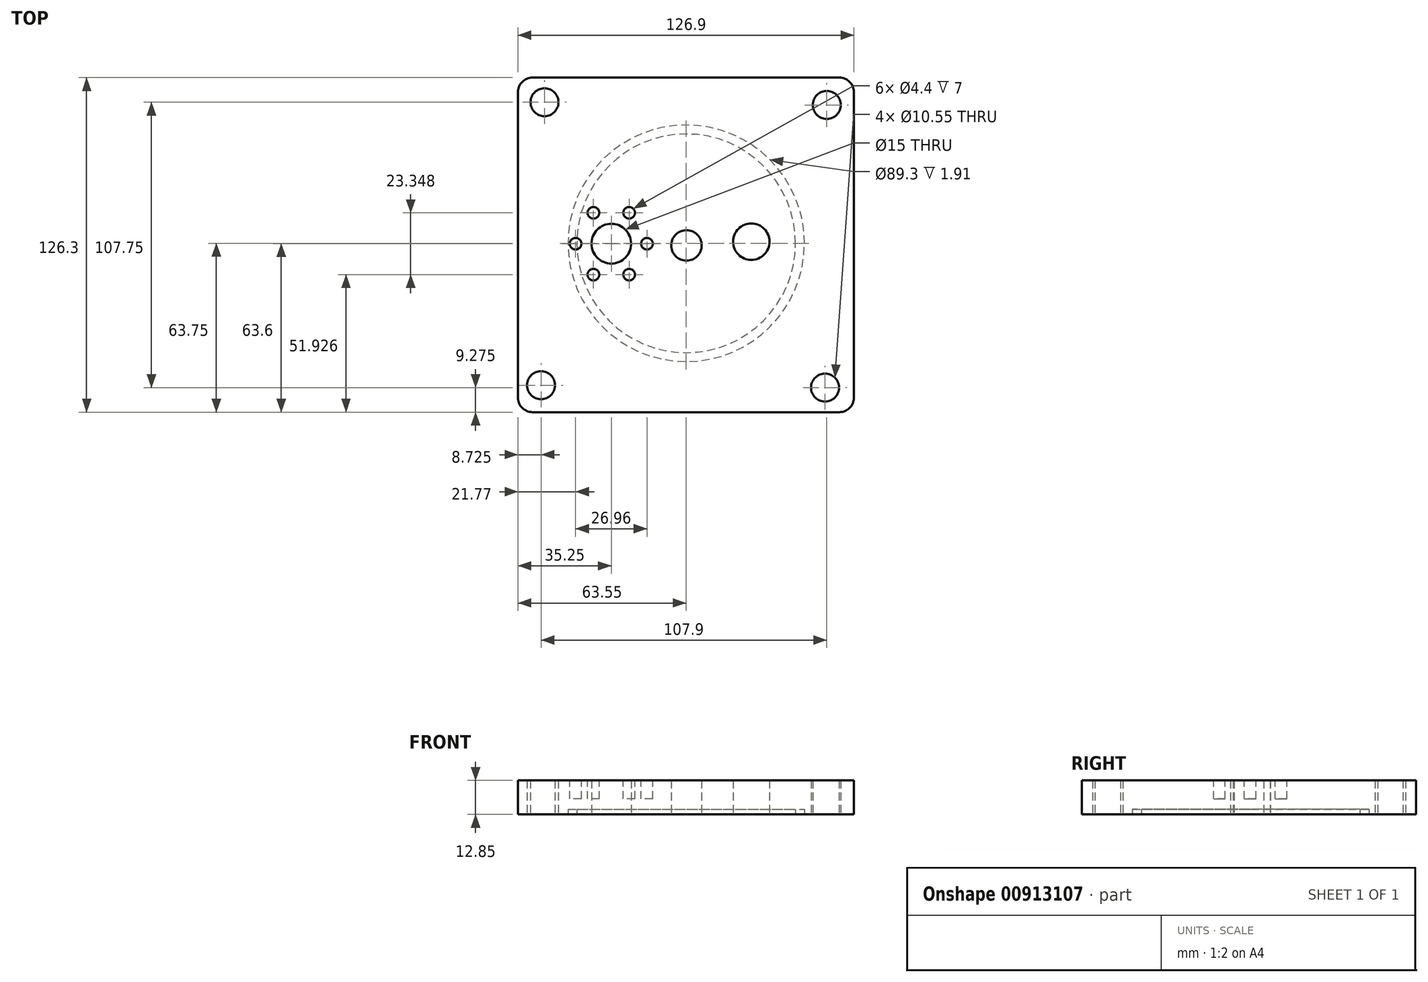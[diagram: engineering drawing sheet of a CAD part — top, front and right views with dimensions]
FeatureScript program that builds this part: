
annotation { "Feature Type Name" : "Feature", "Feature Type Description" : "" }
export const myFeature = defineFeature(function(context is Context, id is Id, definition is map)
    precondition{}
    {
        {
            var Q0;
            Q0=qCreatedBy(makeId("Top.planeOp"),FACE);
            var sketch = newSketch(context, id + "F0", { "sketchPlane" : qUnion([Q0])});
            skLineSegment(sketch, "E0.bottom", {"start": v(57.95, 63.15) * mm, "end": v(-57.95, 63.15) * mm});
            skLineSegment(sketch, "E0.top", {"start": v(57.95, -63.15) * mm, "end": v(-57.95, -63.15) * mm});
            skLineSegment(sketch, "E0.left", {"start": v(63.45, 57.65) * mm, "end": v(63.45, -57.65) * mm});
            skLineSegment(sketch, "E0.right", {"start": v(-63.45, 57.65) * mm, "end": v(-63.45, -57.65) * mm});
            skPoint(sketch, "E0.middle", {"position": v(0, 0) * mm});
            skCircle(sketch, "E1", {"center": v(-28.2, 0.45) * mm, "radius": 7.5 * mm});
            skCircle(sketch, "E2", {"center": v(0.2, -0.2) * mm, "radius": 5.75 * mm});
            skCircle(sketch, "E3", {"center": v(24.68, 1.22) * mm, "radius": 6.88 * mm});
            skCircle(sketch, "E4", {"center": v(-53.42, 53.88) * mm, "radius": 5.28 * mm});
            skCircle(sketch, "E5", {"center": v(53.18, 52.83) * mm, "radius": 5.28 * mm});
            skCircle(sketch, "E6", {"center": v(52.53, -53.88) * mm, "radius": 5.28 * mm});
            skCircle(sketch, "E7", {"center": v(-54.72, -52.98) * mm, "radius": 5.28 * mm});
            skPoint(sketch, "E8.visualSharp", {"position": v(-63.45, 63.15) * mm});
            skArc(sketch, "E8.filletArc", {"start": v(-57.95, 63.15) * mm, "mid": v(-61.84, 61.54) * mm, "end": v(-63.45, 57.65) * mm});
            skPoint(sketch, "E9.visualSharp", {"position": v(63.45, 63.15) * mm});
            skArc(sketch, "E9.filletArc", {"start": v(63.45, 57.65) * mm, "mid": v(61.84, 61.54) * mm, "end": v(57.95, 63.15) * mm});
            skPoint(sketch, "E10.visualSharp", {"position": v(-63.45, -63.15) * mm});
            skArc(sketch, "E10.filletArc", {"start": v(-63.45, -57.65) * mm, "mid": v(-61.84, -61.54) * mm, "end": v(-57.95, -63.15) * mm});
            skPoint(sketch, "E11.visualSharp", {"position": v(63.45, -63.15) * mm});
            skArc(sketch, "E11.filletArc", {"start": v(57.95, -63.15) * mm, "mid": v(61.84, -61.54) * mm, "end": v(63.45, -57.65) * mm});
            skSolve(sketch);
        }
        {
            var Q0;
            Q0=makeQuery(id+"F0.imprint","IMPRINT",FACE,{"disambiguationData":[TD([[makeQuery(id+"F0.imprint","IMPRINT",EDGE,{"derivedFrom":sQuery(id+"F0.wireOp",EDGE,"E0.bottom")}),1.0]])]});
            extrude(context, id + "F1", {"entities" : qUnion([Q0]), "depth" : 12.85 * mm, "offsetDistance" : 25 * mm});
        }
        {
            var Q0;
            Q0=makeQuery(id+"F1.opExtrude","CAP_FACE",FACE,{"disambiguationData":[OSD([sQuery(id+"F0.wireOp",EDGE,"E0.bottom"),sQuery(id+"F0.wireOp",EDGE,"E0.top"),sQuery(id+"F0.wireOp",EDGE,"E0.left"),sQuery(id+"F0.wireOp",EDGE,"E0.right"),sQuery(id+"F0.wireOp",EDGE,"E1"),sQuery(id+"F0.wireOp",EDGE,"E2"),sQuery(id+"F0.wireOp",EDGE,"E3"),sQuery(id+"F0.wireOp",EDGE,"E4"),sQuery(id+"F0.wireOp",EDGE,"E5"),sQuery(id+"F0.wireOp",EDGE,"E6"),sQuery(id+"F0.wireOp",EDGE,"E7"),sQuery(id+"F0.wireOp",EDGE,"E8.filletArc"),sQuery(id+"F0.wireOp",EDGE,"E9.filletArc"),sQuery(id+"F0.wireOp",EDGE,"E10.filletArc"),sQuery(id+"F0.wireOp",EDGE,"E11.filletArc")])],"isStart":true});
            var Q1;
            Q1=makeQuery(id+"F1.opExtrude","CAP_FACE",FACE,{"disambiguationData":[OSD([sQuery(id+"F0.wireOp",EDGE,"E0.bottom"),sQuery(id+"F0.wireOp",EDGE,"E0.top"),sQuery(id+"F0.wireOp",EDGE,"E0.left"),sQuery(id+"F0.wireOp",EDGE,"E0.right"),sQuery(id+"F0.wireOp",EDGE,"E1"),sQuery(id+"F0.wireOp",EDGE,"E2"),sQuery(id+"F0.wireOp",EDGE,"E3"),sQuery(id+"F0.wireOp",EDGE,"E4"),sQuery(id+"F0.wireOp",EDGE,"E5"),sQuery(id+"F0.wireOp",EDGE,"E6"),sQuery(id+"F0.wireOp",EDGE,"E7"),sQuery(id+"F0.wireOp",EDGE,"E8.filletArc"),sQuery(id+"F0.wireOp",EDGE,"E9.filletArc"),sQuery(id+"F0.wireOp",EDGE,"E10.filletArc"),sQuery(id+"F0.wireOp",EDGE,"E11.filletArc")])],"isStart":true});
            var sketch = newSketch(context, id + "F2", { "sketchPlane" : qUnion([Q0, Q1])});
            skCircle(sketch, "E12", {"center": v(0.1, -0.6) * mm, "radius": 44.65 * mm});
            skCircle(sketch, "E13", {"center": v(0.1, -0.6) * mm, "radius": 41.28 * mm});
            skSolve(sketch);
        }
        {
            var Q0;
            Q0 = qSketchRegion(id + "F2", true);
            extrude(context, id + "F3", {"entities" : qUnion([Q0]), "operationType" : NewBodyOperationType.REMOVE, "oppositeDirection" : true, "depth" : 1.91 * mm, "offsetDistance" : 25 * mm});
        }
        {
            var Q0;
            Q0=makeQuery(id+"F1.opExtrude","CAP_FACE",FACE,{"disambiguationData":[OSD([sQuery(id+"F0.wireOp",EDGE,"E0.bottom"),sQuery(id+"F0.wireOp",EDGE,"E0.top"),sQuery(id+"F0.wireOp",EDGE,"E0.left"),sQuery(id+"F0.wireOp",EDGE,"E0.right"),sQuery(id+"F0.wireOp",EDGE,"E1"),sQuery(id+"F0.wireOp",EDGE,"E2"),sQuery(id+"F0.wireOp",EDGE,"E3"),sQuery(id+"F0.wireOp",EDGE,"E4"),sQuery(id+"F0.wireOp",EDGE,"E5"),sQuery(id+"F0.wireOp",EDGE,"E6"),sQuery(id+"F0.wireOp",EDGE,"E7"),sQuery(id+"F0.wireOp",EDGE,"E8.filletArc"),sQuery(id+"F0.wireOp",EDGE,"E9.filletArc"),sQuery(id+"F0.wireOp",EDGE,"E10.filletArc"),sQuery(id+"F0.wireOp",EDGE,"E11.filletArc")])],"isStart":false});
            var sketch = newSketch(context, id + "F4", { "sketchPlane" : qUnion([Q0])});
            skCircle(sketch, "E14", {"center": v(-28.2, 0.45) * mm, "radius": 7.5 * mm, "construction": true});
            skLineSegment(sketch, "E15", {"start": v(-63.45, 0.45) * mm, "end": v(63.45, 0.45) * mm, "construction": true});
            skCircle(sketch, "E16", {"center": v(-14.72, 0.45) * mm, "radius": 2.2 * mm});
            skCircle(sketch, "E17.1.0", {"center": v(-21.46, 12.12) * mm, "radius": 2.2 * mm});
            skCircle(sketch, "E17.2.0", {"center": v(-34.94, 12.12) * mm, "radius": 2.2 * mm});
            skCircle(sketch, "E17.3.0", {"center": v(-41.68, 0.45) * mm, "radius": 2.2 * mm});
            skCircle(sketch, "E17.4.0", {"center": v(-34.94, -11.22) * mm, "radius": 2.2 * mm});
            skCircle(sketch, "E17.5.0", {"center": v(-21.46, -11.22) * mm, "radius": 2.2 * mm});
            skSolve(sketch);
        }
        {
            var Q0;
            Q0=makeQuery(id+"F4.imprint","IMPRINT",FACE,{"disambiguationData":[TD([[makeQuery(id+"F4.imprint","IMPRINT",EDGE,{"derivedFrom":sQuery(id+"F4.wireOp",EDGE,"E17.1.0")}),1.0]])]});
            var Q1;
            Q1=makeQuery(id+"F4.imprint","IMPRINT",FACE,{"disambiguationData":[TD([[makeQuery(id+"F4.imprint","IMPRINT",EDGE,{"derivedFrom":sQuery(id+"F4.wireOp",EDGE,"E17.2.0")}),1.0]])]});
            var Q2;
            Q2=makeQuery(id+"F4.imprint","IMPRINT",FACE,{"disambiguationData":[TD([[makeQuery(id+"F4.imprint","IMPRINT",EDGE,{"derivedFrom":sQuery(id+"F4.wireOp",EDGE,"E17.3.0")}),1.0]])]});
            var Q3;
            Q3=makeQuery(id+"F4.imprint","IMPRINT",FACE,{"disambiguationData":[TD([[makeQuery(id+"F4.imprint","IMPRINT",EDGE,{"derivedFrom":sQuery(id+"F4.wireOp",EDGE,"E17.4.0")}),1.0]])]});
            var Q4;
            Q4=makeQuery(id+"F4.imprint","IMPRINT",FACE,{"disambiguationData":[TD([[makeQuery(id+"F4.imprint","IMPRINT",EDGE,{"derivedFrom":sQuery(id+"F4.wireOp",EDGE,"E17.5.0")}),1.0]])]});
            var Q5;
            Q5=makeQuery(id+"F4.imprint","IMPRINT",FACE,{"disambiguationData":[TD([[makeQuery(id+"F4.imprint","IMPRINT",EDGE,{"derivedFrom":sQuery(id+"F4.wireOp",EDGE,"E16")}),1.0]])]});
            extrude(context, id + "F5", {"entities" : qUnion([Q0, Q1, Q2, Q3, Q4, Q5]), "operationType" : NewBodyOperationType.REMOVE, "oppositeDirection" : true, "depth" : 7 * mm, "offsetDistance" : 25 * mm});
        }
    });
